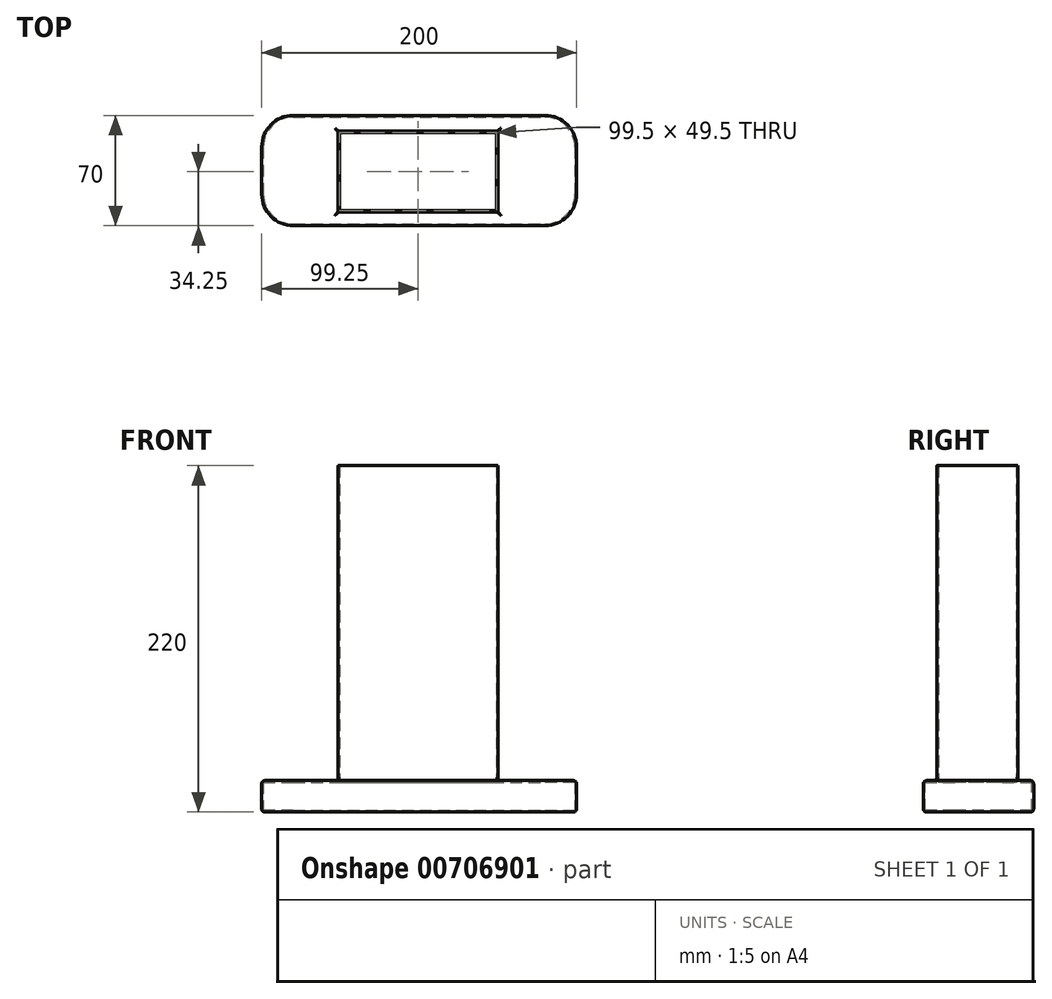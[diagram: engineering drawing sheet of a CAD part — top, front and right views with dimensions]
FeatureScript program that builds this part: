
annotation { "Feature Type Name" : "Feature", "Feature Type Description" : "" }
export const myFeature = defineFeature(function(context is Context, id is Id, definition is map)
    precondition{}
    {
        {
            var Q0;
            Q0=qCreatedBy(makeId("Top.planeOp"),FACE);
            var sketch = newSketch(context, id + "F0", { "sketchPlane" : qUnion([Q0])});
            skLineSegment(sketch, "E0.bottom", {"start": v(-80, 35) * mm, "end": v(80, 35) * mm});
            skLineSegment(sketch, "E0.top", {"start": v(-80, -35) * mm, "end": v(80, -35) * mm});
            skLineSegment(sketch, "E0.left", {"start": v(-100, 15) * mm, "end": v(-100, -15) * mm});
            skLineSegment(sketch, "E0.right", {"start": v(100, 15) * mm, "end": v(100, -15) * mm});
            skPoint(sketch, "E1.visualSharp", {"position": v(-100, 35) * mm});
            skArc(sketch, "E1.filletArc", {"start": v(-80, 35) * mm, "mid": v(-94.14, 29.14) * mm, "end": v(-100, 15) * mm});
            skPoint(sketch, "E2.visualSharp", {"position": v(-100, -35) * mm});
            skArc(sketch, "E2.filletArc", {"start": v(-100, -15) * mm, "mid": v(-94.14, -29.14) * mm, "end": v(-80, -35) * mm});
            skPoint(sketch, "E3.visualSharp", {"position": v(100, 35) * mm});
            skArc(sketch, "E3.filletArc", {"start": v(100, 15) * mm, "mid": v(94.14, 29.14) * mm, "end": v(80, 35) * mm});
            skPoint(sketch, "E4.visualSharp", {"position": v(100, -35) * mm});
            skArc(sketch, "E4.filletArc", {"start": v(80, -35) * mm, "mid": v(94.14, -29.14) * mm, "end": v(100, -15) * mm});
            skSolve(sketch);
        }
        {
            var Q0;
            Q0=makeQuery(id+"F0.imprint","IMPRINT",FACE,{"disambiguationData":[TD([[makeQuery(id+"F0.imprint","IMPRINT",EDGE,{"derivedFrom":sQuery(id+"F0.wireOp",EDGE,"E0.bottom")}),-1.0]])]});
            extrude(context, id + "F1", {"entities" : qUnion([Q0]), "depth" : 20 * mm, "offsetDistance" : 25 * mm});
        }
        {
            var Q0;
            Q0=makeQuery(id+"F1.opExtrude","CAP_FACE",FACE,{"disambiguationData":[OSD([sQuery(id+"F0.wireOp",EDGE,"E0.bottom"),sQuery(id+"F0.wireOp",EDGE,"E0.top"),sQuery(id+"F0.wireOp",EDGE,"E0.left"),sQuery(id+"F0.wireOp",EDGE,"E0.right"),sQuery(id+"F0.wireOp",EDGE,"E1.filletArc"),sQuery(id+"F0.wireOp",EDGE,"E2.filletArc"),sQuery(id+"F0.wireOp",EDGE,"E3.filletArc"),sQuery(id+"F0.wireOp",EDGE,"E4.filletArc")])],"isStart":false});
            var sketch = newSketch(context, id + "F2", { "sketchPlane" : qUnion([Q0])});
            skLineSegment(sketch, "E5.bottom", {"start": v(-51.5, 25) * mm, "end": v(50, 25) * mm});
            skLineSegment(sketch, "E5.top", {"start": v(-51.5, -26.5) * mm, "end": v(50, -26.5) * mm});
            skLineSegment(sketch, "E5.left", {"start": v(-51.5, 25) * mm, "end": v(-51.5, -26.5) * mm});
            skLineSegment(sketch, "E5.right", {"start": v(50, 25) * mm, "end": v(50, -26.5) * mm});
            skSolve(sketch);
        }
        {
            var Q0;
            Q0=makeQuery(id+"F2.imprint","IMPRINT",FACE,{"disambiguationData":[TD([[makeQuery(id+"F2.imprint","IMPRINT",EDGE,{"derivedFrom":sQuery(id+"F2.wireOp",EDGE,"E5.bottom")}),-1.0]])]});
            extrude(context, id + "F3", {"entities" : qUnion([Q0]), "operationType" : NewBodyOperationType.ADD, "depth" : 200 * mm, "offsetDistance" : 25 * mm});
        }
        {
            var Q0;
            Q0=makeQuery(id+"F3.opExtrude","CAP_FACE",FACE,{"disambiguationData":[OSD([sQuery(id+"F2.wireOp",EDGE,"E5.bottom"),sQuery(id+"F2.wireOp",EDGE,"E5.top"),sQuery(id+"F2.wireOp",EDGE,"E5.left"),sQuery(id+"F2.wireOp",EDGE,"E5.right")])],"isStart":false});
            shell(context, id + "F4", {"entities" : qUnion([Q0]), "thickness" : 1 * mm});
        }
        {
            var Q0;
            Q0=makeQuery(id+"F1.opExtrude","CAP_EDGE",EDGE,{"disambiguationData":[OSD([sQuery(id+"F0.wireOp",EDGE,"E4.filletArc")])],"isStart":false});
            var Q1;
            Q1=makeQuery(id+"F1.opExtrude","CAP_FACE",FACE,{"disambiguationData":[OSD([sQuery(id+"F0.wireOp",EDGE,"E0.bottom"),sQuery(id+"F0.wireOp",EDGE,"E0.top"),sQuery(id+"F0.wireOp",EDGE,"E0.left"),sQuery(id+"F0.wireOp",EDGE,"E0.right"),sQuery(id+"F0.wireOp",EDGE,"E1.filletArc"),sQuery(id+"F0.wireOp",EDGE,"E2.filletArc"),sQuery(id+"F0.wireOp",EDGE,"E3.filletArc"),sQuery(id+"F0.wireOp",EDGE,"E4.filletArc")])],"isStart":false});
            var Q2;
            Q2=makeQuery(id+"F1.opExtrude","CAP_EDGE",EDGE,{"disambiguationData":[OSD([sQuery(id+"F0.wireOp",EDGE,"E3.filletArc")])],"isStart":false});
            var Q3;
            Q3=makeQuery(id+"F1.opExtrude","CAP_EDGE",EDGE,{"disambiguationData":[OSD([sQuery(id+"F0.wireOp",EDGE,"E0.bottom")])],"isStart":false});
            var Q4;
            Q4=makeQuery(id+"F1.opExtrude","CAP_EDGE",EDGE,{"disambiguationData":[OSD([sQuery(id+"F0.wireOp",EDGE,"E1.filletArc")])],"isStart":false});
            var Q5;
            Q5=makeQuery(id+"F1.opExtrude","CAP_EDGE",EDGE,{"disambiguationData":[OSD([sQuery(id+"F0.wireOp",EDGE,"E0.left")])],"isStart":false});
            var Q6;
            Q6=makeQuery(id+"F1.opExtrude","CAP_EDGE",EDGE,{"disambiguationData":[OSD([sQuery(id+"F0.wireOp",EDGE,"E2.filletArc")])],"isStart":false});
            var Q7;
            Q7=makeQuery(id+"F1.opExtrude","SWEPT_FACE",FACE,{"disambiguationData":[OSD([sQuery(id+"F0.wireOp",EDGE,"E3.filletArc")])]});
            var Q8;
            Q8=makeQuery(id+"F1.opExtrude","SWEPT_FACE",FACE,{"disambiguationData":[OSD([sQuery(id+"F0.wireOp",EDGE,"E0.bottom")])]});
            var Q9;
            Q9=makeQuery(id+"F1.opExtrude","SWEPT_FACE",FACE,{"disambiguationData":[OSD([sQuery(id+"F0.wireOp",EDGE,"E1.filletArc")])]});
            var Q10;
            Q10=makeQuery(id+"F1.opExtrude","SWEPT_FACE",FACE,{"disambiguationData":[OSD([sQuery(id+"F0.wireOp",EDGE,"E0.left")])]});
            var Q11;
            Q11=makeQuery(id+"F1.opExtrude","SWEPT_FACE",FACE,{"disambiguationData":[OSD([sQuery(id+"F0.wireOp",EDGE,"E2.filletArc")])]});
            var Q12;
            Q12=makeQuery(id+"F1.opExtrude","SWEPT_FACE",FACE,{"disambiguationData":[OSD([sQuery(id+"F0.wireOp",EDGE,"E0.top")])]});
            fillet(context, id + "F5", {"entities" : qUnion([Q0, Q1, Q2, Q3, Q4, Q5, Q6, Q7, Q8, Q9, Q10, Q11, Q12]), "radius" : 2 * mm, "tangentPropagation" : true, "allowEdgeOverflow" : false});
        }
        {
            var Q0;
            Q0=makeQuery(id+"F3.opExtrude","SWEPT_EDGE",EDGE,{"disambiguationData":[OSD([sQuery(id+"F2.wireOp",EDGE,"E5.top"),sQuery(id+"F2.wireOp",EDGE,"E5.left")])]});
            var Q1;
            Q1=makeQuery(id+"F3.opExtrude","SWEPT_EDGE",EDGE,{"disambiguationData":[OSD([sQuery(id+"F2.wireOp",EDGE,"E5.bottom"),sQuery(id+"F2.wireOp",EDGE,"E5.left")])]});
            var Q2;
            Q2=makeQuery(id+"F3.opExtrude","SWEPT_EDGE",EDGE,{"disambiguationData":[OSD([sQuery(id+"F2.wireOp",EDGE,"E5.top"),sQuery(id+"F2.wireOp",EDGE,"E5.right")])]});
            var Q3;
            Q3=makeQuery(id+"F3.opExtrude","SWEPT_EDGE",EDGE,{"disambiguationData":[OSD([sQuery(id+"F2.wireOp",EDGE,"E5.bottom"),sQuery(id+"F2.wireOp",EDGE,"E5.right")])]});
            fillet(context, id + "F6", {"entities" : qUnion([Q0, Q1, Q2, Q3]), "radius" : 0.5 * mm, "tangentPropagation" : true, "allowEdgeOverflow" : false});
        }
    });
